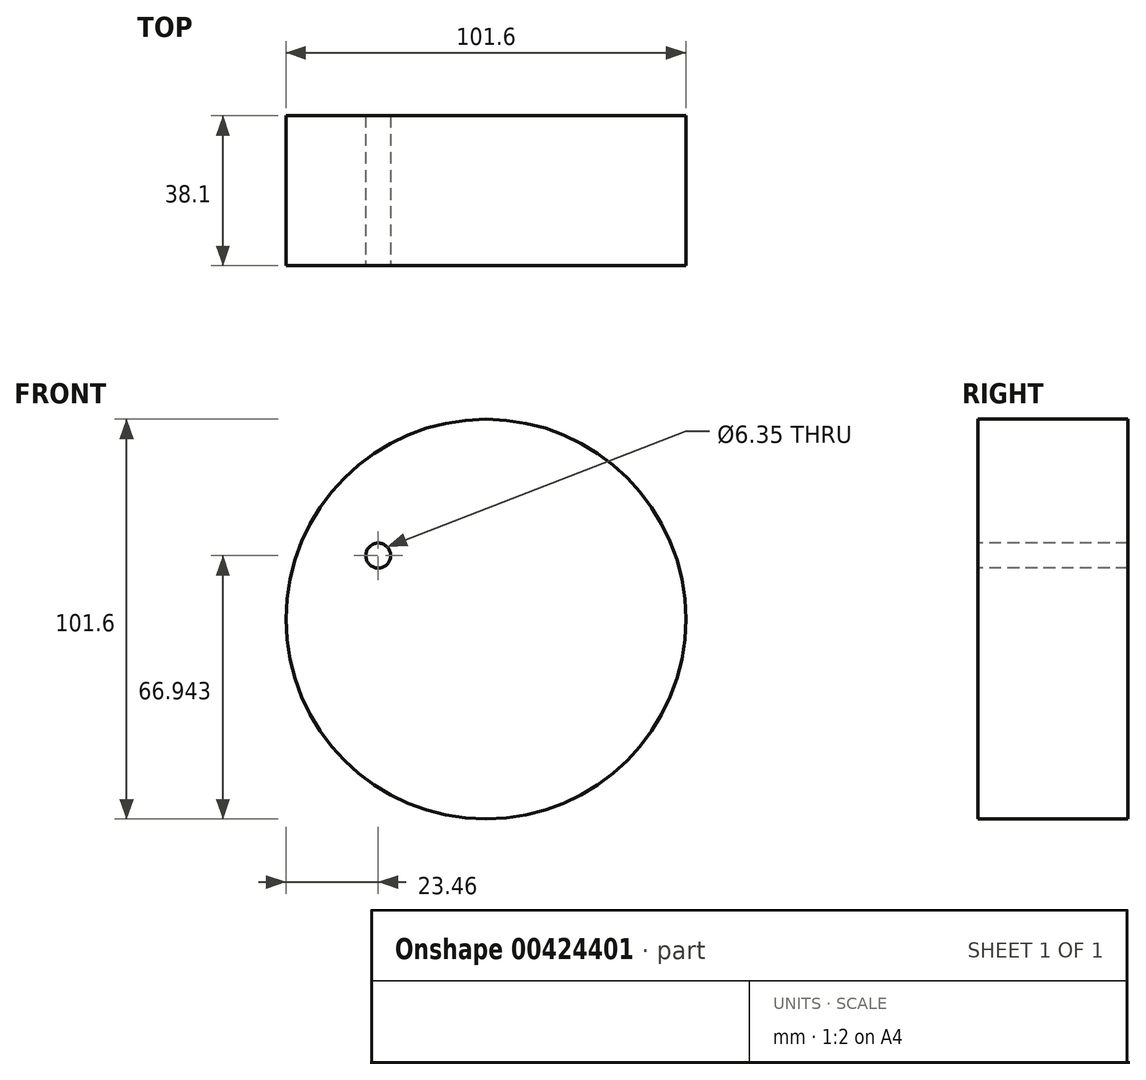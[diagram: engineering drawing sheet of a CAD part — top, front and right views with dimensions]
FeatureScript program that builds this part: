
annotation { "Feature Type Name" : "Feature", "Feature Type Description" : "" }
export const myFeature = defineFeature(function(context is Context, id is Id, definition is map)
    precondition{}
    {
        {
            var Q0;
            Q0=qCreatedBy(makeId("Front.planeOp"),FACE);
            var sketch = newSketch(context, id + "F0", { "sketchPlane" : qUnion([Q0])});
            skCircle(sketch, "E0", {"center": v(0, 0) * mm, "radius": 50.8 * mm});
            skSolve(sketch);
        }
        {
            var Q0;
            Q0=makeQuery(id+"F0.imprint","IMPRINT",FACE,{"disambiguationData":[TD([[makeQuery(id+"F0.imprint","IMPRINT",EDGE,{"derivedFrom":sQuery(id+"F0.wireOp",EDGE,"E0")}),1.0]])]});
            extrude(context, id + "F1", {"entities" : qUnion([Q0]), "depth" : 38.1 * mm});
        }
        {
            var Q0;
            Q0=makeQuery(id+"F1.opExtrude","CAP_FACE",FACE,{"disambiguationData":[OSD([sQuery(id+"F0.wireOp",EDGE,"E0")])],"isStart":false});
            var sketch = newSketch(context, id + "F2", { "sketchPlane" : qUnion([Q0])});
            skCircle(sketch, "E1", {"center": v(0, 0) * mm, "radius": 31.75 * mm});
            skCircle(sketch, "E2", {"center": v(0, 31.75) * mm, "radius": 3.18 * mm});
            skCircle(sketch, "E3", {"center": v(-27.34, 16.14) * mm, "radius": 4.76 * mm});
            skCircle(sketch, "E4", {"center": v(26.43, 17.59) * mm, "radius": 9.53 * mm});
            skSolve(sketch);
        }
        {
            var Q0;
            Q0=sQuery(id+"F2.wireOp",VERTEX,"E3.center");
            var Q1;
            Q1=makeQuery(id+"F1.opExtrude","SWEPT_BODY",BODY,{"disambiguationData":[OSD([sQuery(id+"F0.wireOp",EDGE,"E0")])]});
            hole(context, id + "F3", {"style" : HoleStyle.SIMPLE, "endStyle" : HoleEndStyle.THROUGH, "holeDiameter" : 6.35 * mm, "isTappedThrough" : true, "tappedDepth" : 12.7 * mm, "tapClearance" : 3, "locations" : qUnion([Q0]), "scope" : qUnion([Q1])});
        }
    });
